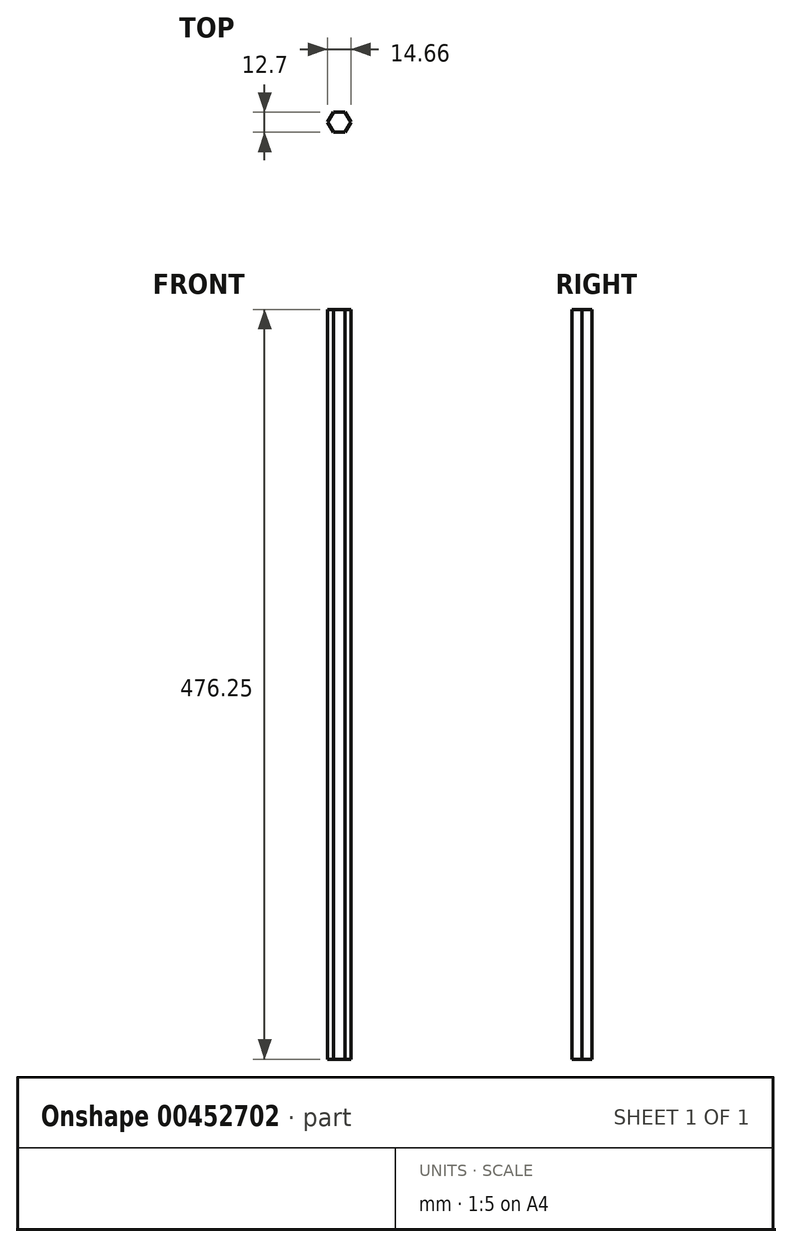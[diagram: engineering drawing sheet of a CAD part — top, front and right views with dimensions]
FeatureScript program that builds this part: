
annotation { "Feature Type Name" : "Feature", "Feature Type Description" : "" }
export const myFeature = defineFeature(function(context is Context, id is Id, definition is map)
    precondition{}
    {
        {
            var Q0;
            Q0=qCreatedBy(makeId("Top.planeOp"),FACE);
            var sketch = newSketch(context, id + "F0", { "sketchPlane" : qUnion([Q0])});
            skCircle(sketch, "E0.cCircle", {"center": v(0, 0) * mm, "radius": 6.35 * mm, "construction": true});
            skLineSegment(sketch, "E0.0", {"start": v(-3.67, 6.35) * mm, "end": v(3.67, 6.35) * mm});
            skLineSegment(sketch, "E0.1", {"start": v(3.67, 6.35) * mm, "end": v(7.33, 0) * mm});
            skLineSegment(sketch, "E0.2", {"start": v(7.33, 0) * mm, "end": v(3.67, -6.35) * mm});
            skLineSegment(sketch, "E0.3", {"start": v(3.67, -6.35) * mm, "end": v(-3.67, -6.35) * mm});
            skLineSegment(sketch, "E0.4", {"start": v(-3.67, -6.35) * mm, "end": v(-7.33, 0) * mm});
            skLineSegment(sketch, "E0.5", {"start": v(-7.33, 0) * mm, "end": v(-3.67, 6.35) * mm});
            skPoint(sketch, "E0.0.midPoint", {"position": v(0, 6.35) * mm});
            skSolve(sketch);
        }
        {
            var Q0;
            Q0 = qSketchRegion(id + "F0", true);
            extrude(context, id + "F1", {"entities" : qUnion([Q0]), "depth" : 476.25 * mm});
        }
    });
